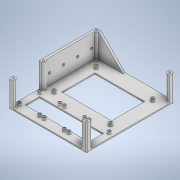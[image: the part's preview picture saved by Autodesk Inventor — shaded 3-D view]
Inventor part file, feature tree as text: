
AUTODESK INVENTOR PART (.ipt)
format: ipt  version: 2020 (Build 240168000, 168)  size: 418,304 bytes
history: native  units: in
note: dims shown in document units (in); Inventor stores cm internally (conversion verified against a paired STEP export)
features: extrude x16, sketch x16, fillet x4, mirror x1, chamfer x1
ambient origin geometry x8: Origin, YZ Plane, XZ Plane, XY Plane, X Axis, Y Axis, Z Axis, Center Point
bodies: Solid1 (feature_tree)
feature tree (38):
  extrude  "Extrusion1"  Depth=4.5276in
  extrude  "Extrusion2"  Depth=0.1575in
  extrude  "Extrusion3"  Depth=0.2756in
  extrude  "Extrusion4"  Depth=1.498in
  extrude  "Extrusion5"  Depth=1.498in
  extrude  "Extrusion6"  Depth=2.0049in
  mirror  "Mirror1"
  extrude  "Extrusion7"  Depth=2.0049in
  extrude  "Extrusion8"  Depth=0.1575in TaperAngle=0.0deg
  fillet  "Fillet1"  Radius=0.1575in
  extrude  "Extrusion9"  Depth=0.1575in
  fillet  "Fillet2"  Radius=0.1575in
  extrude  "Extrusion10"  Depth=1.6875in TaperAngle=0.0deg
  extrude  "Extrusion11"  Depth=0.2362in
  chamfer  "Chamfer1"  Distance=0.1575in
  extrude  "Extrusion12"  Depth=0.1575in
  fillet  "Fillet4"  Radius=0.1575in
  extrude  "Extrusion13"  Depth=0.1575in
  extrude  "Extrusion14"  Depth=0.1575in
  extrude  "Extrusion15"  Depth=0.1575in
  extrude  "Extrusion16"  Depth=0.0787in TaperAngle=0.0deg
  fillet  "Fillet5"  Radius=3.5433in
  sketch  "Sketch1"  dims[d0=5.5118in d1=4.5276in]
  sketch  "Sketch2"  dims[d2=0.1575in d3=0.0in d4=0.2756in]
  sketch  "Sketch3"  dims[d5=0.2756in d6=0.2756in]
  sketch  "Sketch4"  dims[d7=0.2756in d8=1.498in]
  sketch  "Sketch6"  dims[d9=2.9961in d10=1.498in]
  sketch  "Sketch7"  dims[d11=2.9961in d12=2.0049in]
  sketch  "Sketch8"  dims[d13=4.0098in d14=2.0049in]
  sketch  "Sketch9"  dims[d15=4.0098in d16=0.1575in d17=0.0in d18=0.1575in]
  sketch  "Sketch10"  dims[d19=0.1575in d20=0.1575in d21=0.1575in]
  sketch  "Sketch11"  dims[d22=0.7874in d23=0.0in d24=1.6875in d25=0.0in]
  sketch  "Sketch12"  dims[d31=0.2362in d32=0.2362in]
  sketch  "Sketch13"  dims[d34=0.2362in]
  sketch  "Sketch14"  dims[d35=0.2362in]
  sketch  "Sketch15"  dims[d36=0.2362in]
  sketch  "Sketch16"  dims[d37=0.2362in d38=0.1575in d39=0.0in]
  sketch  "Sketch17"  dims[d40=0.1575in d41=0.1575in d42=0.1575in d43=0.1575in d44=0.1575in d45=0.1575in d46=0.7874in d47=0.0in d48=3.5433in d49=2.3622in d50=4.5487in d51=1.0438in d52=0.7874in d53=0.0in d54=0.315in d55=0.315in d56=0.315in d57=0.315in d58=0.315in d59=0.315in d60=0.315in d61=0.315in d62=1.7323in d63=0.0in d64=0.1575in d65=0.1575in d66=0.1575in d67=0.1575in d68=0.1575in d69=2.3622in d70=0.0in d71=0.0787in d72=0.1575in d73=3.7402in d74=1.7323in d75=0.0in d76=0.3406in d77=0.3406in d78=0.3406in d79=0.3406in d80=0.1969in d81=0.0in d83=0.0591in d84=0.0787in d85=45.0deg d86=0.315in d87=0.315in d88=1.7323in d89=0.0in d90=0.1575in d91=0.1575in d92=2.3622in d93=0.0in d94=0.1575in d95=0.1575in d96=0.1575in d97=0.1575in d98=0.5906in d99=0.0in d100=0.0in d101=1.7323in d102=0.1575in d103=1.7323in d104=0.0in d105=1.7323in d106=0.0in d107=0.0787in d26=0.0197in d27=0.0344in]
